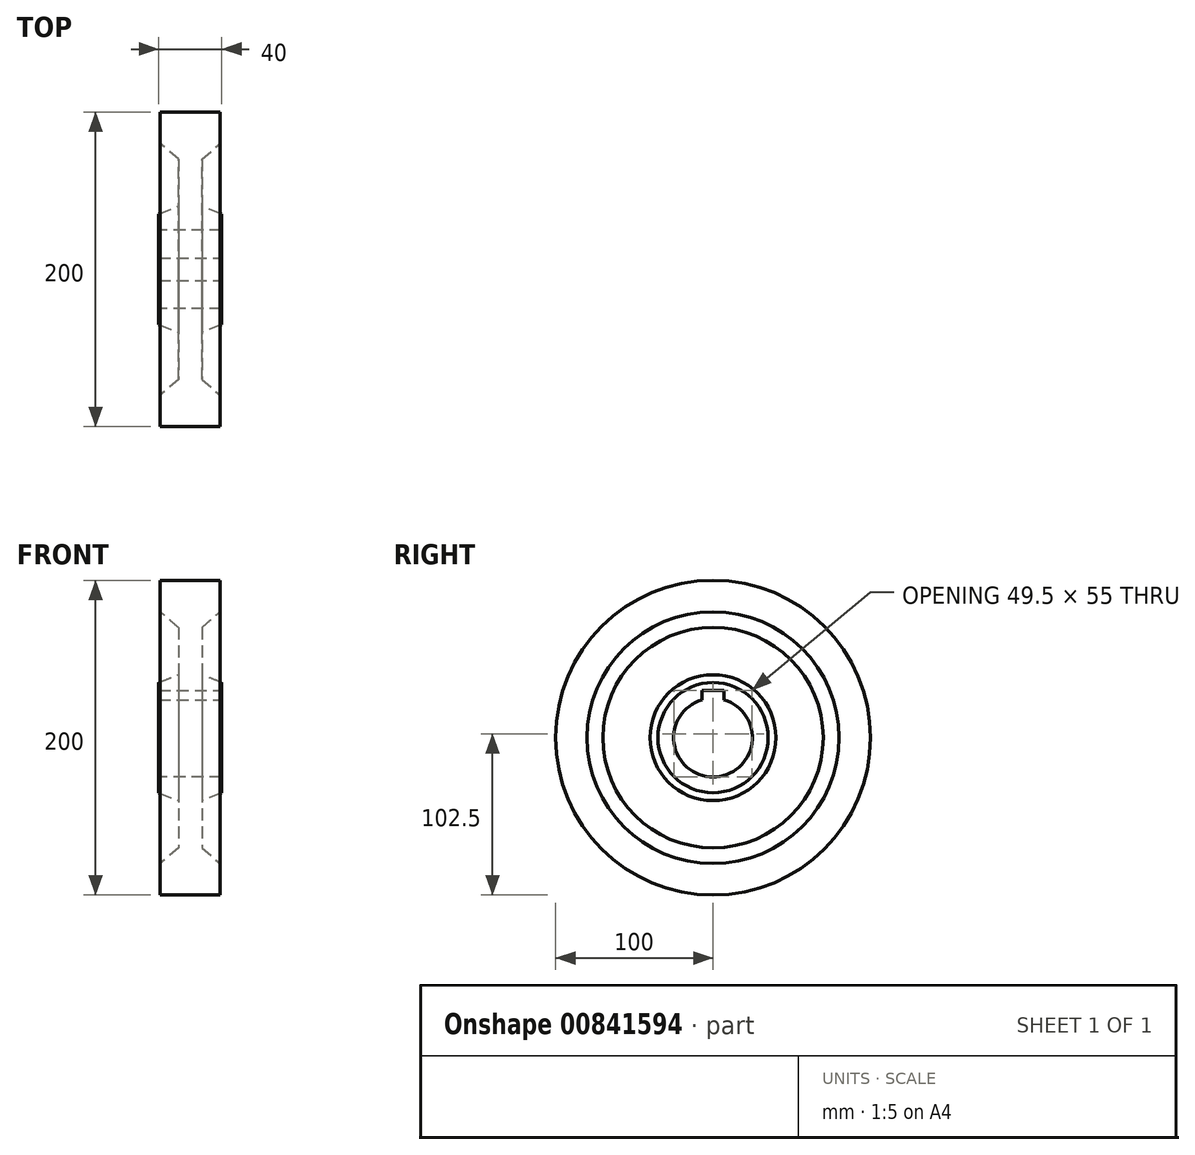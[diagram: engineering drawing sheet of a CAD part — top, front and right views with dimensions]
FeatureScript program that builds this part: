
annotation { "Feature Type Name" : "Feature", "Feature Type Description" : "" }
export const myFeature = defineFeature(function(context is Context, id is Id, definition is map)
    precondition{}
    {
        {
            var Q0;
            Q0=qCreatedBy(makeId("Front.planeOp"),FACE);
            var sketch = newSketch(context, id + "F0", { "sketchPlane" : qUnion([Q0])});
            skLineSegment(sketch, "E0", {"start": v(0, 0) * mm, "end": v(43.92, 0) * mm, "construction": true});
            skLineSegment(sketch, "E1", {"start": v(0, 25) * mm, "end": v(20, 25) * mm});
            skLineSegment(sketch, "E2", {"start": v(20, 25) * mm, "end": v(20, 35) * mm});
            skLineSegment(sketch, "E3", {"start": v(20, 35) * mm, "end": v(7.5, 40) * mm});
            skLineSegment(sketch, "E4", {"start": v(7.5, 40) * mm, "end": v(7.5, 70) * mm});
            skLineSegment(sketch, "E5", {"start": v(7.5, 70) * mm, "end": v(19, 80) * mm});
            skLineSegment(sketch, "E6", {"start": v(19, 80) * mm, "end": v(19, 100) * mm});
            skLineSegment(sketch, "E7", {"start": v(19, 100) * mm, "end": v(0, 100) * mm});
            skLineSegment(sketch, "E8", {"start": v(0, 100) * mm, "end": v(0, 25) * mm, "construction": true});
            skLineSegment(sketch, "E9.MirrorCS", {"start": v(-19, 100) * mm, "end": v(0, 100) * mm});
            skLineSegment(sketch, "E10.MirrorCS", {"start": v(-19, 80) * mm, "end": v(-19, 100) * mm});
            skLineSegment(sketch, "E11.MirrorCS", {"start": v(-7.5, 70) * mm, "end": v(-19, 80) * mm});
            skLineSegment(sketch, "E12.MirrorCS", {"start": v(-7.5, 40) * mm, "end": v(-7.5, 70) * mm});
            skLineSegment(sketch, "E13.MirrorCS", {"start": v(-20, 35) * mm, "end": v(-7.5, 40) * mm});
            skLineSegment(sketch, "E14.MirrorCS", {"start": v(-20, 25) * mm, "end": v(-20, 35) * mm});
            skLineSegment(sketch, "E15.MirrorCS", {"start": v(0, 25) * mm, "end": v(-20, 25) * mm});
            skSolve(sketch);
        }
        {
            var Q0;
            Q0=makeQuery(id+"F0.imprint","IMPRINT",FACE,{"disambiguationData":[TD([[makeQuery(id+"F0.imprint","IMPRINT",EDGE,{"derivedFrom":sQuery(id+"F0.wireOp",EDGE,"E1")}),1.0]])]});
            var Q1;
            Q1=sQuery(id+"F0.wireOp",EDGE,"E0");
            revolve(context, id + "F1", {"surfaceOperationType" : NewSurfaceOperationType.NEW, "entities" : qUnion([Q0]), "axis" : qUnion([Q1]), "revolveType" : RevolveType.FULL});
        }
        {
            var Q0;
            Q0=makeQuery(id+"F1.opRevolve","SWEPT_FACE",FACE,{"disambiguationData":[OSD([sQuery(id+"F0.wireOp",EDGE,"E2")])]});
            var sketch = newSketch(context, id + "F2", { "sketchPlane" : qUnion([Q0])});
            skLineSegment(sketch, "E16.bottom", {"start": v(7, 30) * mm, "end": v(-7, 30) * mm});
            skLineSegment(sketch, "E16.top", {"start": v(7, 20) * mm, "end": v(-7, 20) * mm});
            skLineSegment(sketch, "E16.left", {"start": v(7, 30) * mm, "end": v(7, 20) * mm});
            skLineSegment(sketch, "E16.right", {"start": v(-7, 30) * mm, "end": v(-7, 20) * mm});
            skPoint(sketch, "E16.middle", {"position": v(0, 25) * mm});
            skSolve(sketch);
        }
        {
            var Q0;
            {var subQ0=sQuery(id+"F2.wireOp",EDGE,"E16.bottom");Q0=makeQuery(id+"F2.imprint","IMPRINT",FACE,{"disambiguationData":[TD([[makeQuery(id+"F2.imprint","IMPRINT",EDGE,{"derivedFrom":subQ0}),1.0]])]});}
            extrude(context, id + "F3", {"entities" : qUnion([Q0]), "operationType" : NewBodyOperationType.REMOVE, "endBound" : BoundingType.THROUGH_ALL, "oppositeDirection" : true, "depth" : 25 * mm, "offsetDistance" : 25 * mm});
        }
    });
